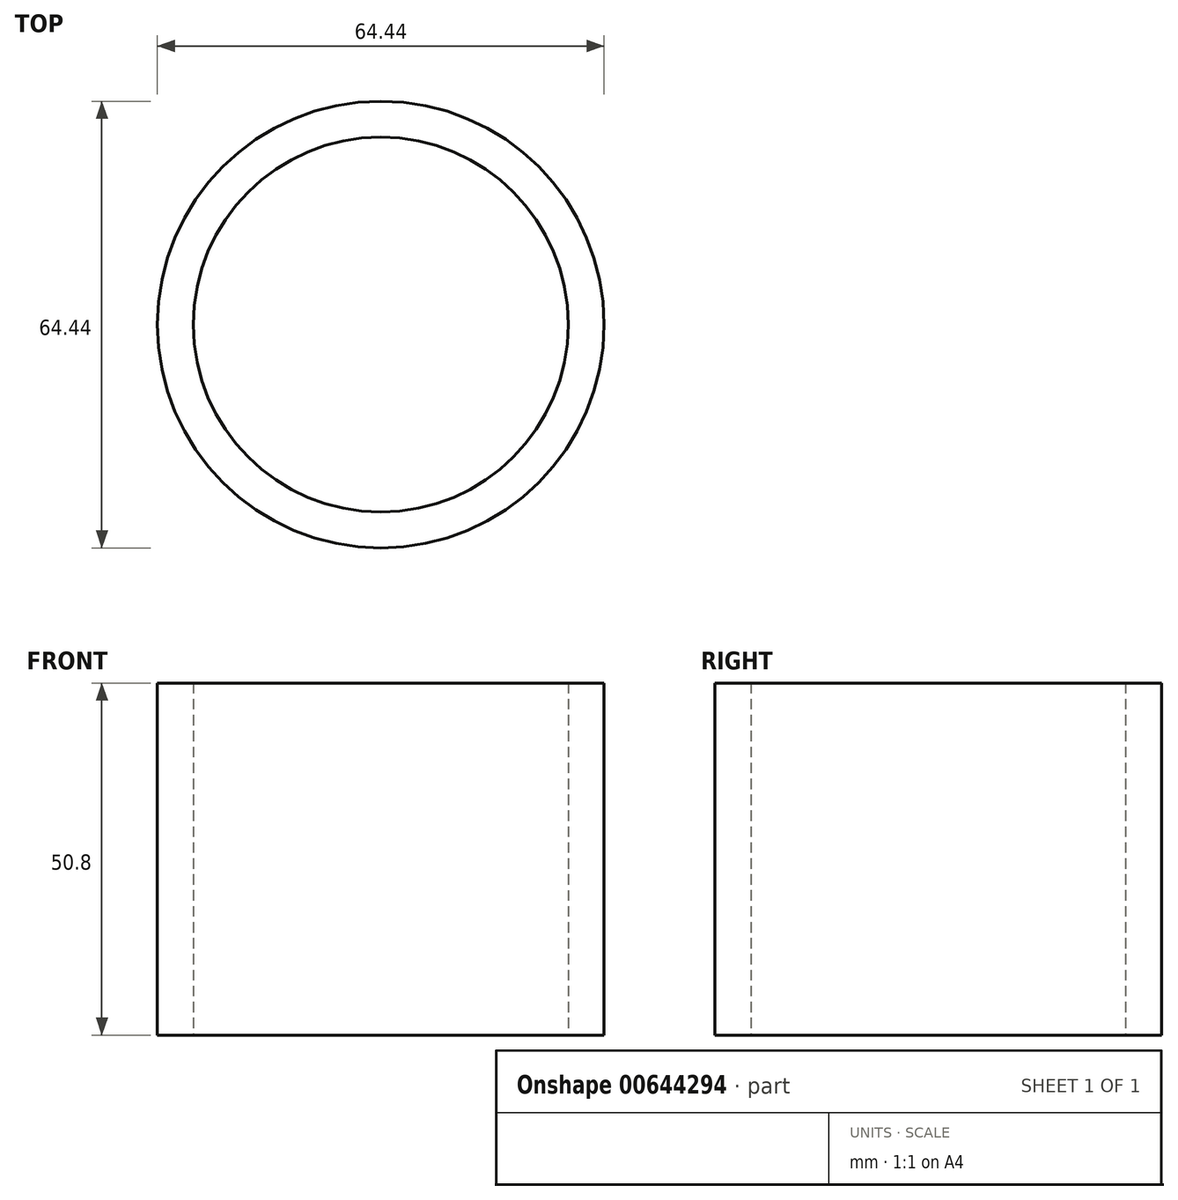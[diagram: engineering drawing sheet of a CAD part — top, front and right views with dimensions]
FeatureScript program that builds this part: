
annotation { "Feature Type Name" : "Feature", "Feature Type Description" : "" }
export const myFeature = defineFeature(function(context is Context, id is Id, definition is map)
    precondition{}
    {
        {
            var Q0;
            Q0=qCreatedBy(makeId("Top.planeOp"),FACE);
            var sketch = newSketch(context, id + "F0", { "sketchPlane" : qUnion([Q0])});
            skCircle(sketch, "E0", {"center": v(0, 0) * mm, "radius": 32.22 * mm});
            skCircle(sketch, "E1", {"center": v(0, 0) * mm, "radius": 27.05 * mm});
            skSolve(sketch);
        }
        {
            var Q0;
            Q0=makeQuery(id+"F0.imprint","IMPRINT",FACE,{"disambiguationData":[TD([[makeQuery(id+"F0.imprint","IMPRINT",EDGE,{"derivedFrom":sQuery(id+"F0.wireOp",EDGE,"E0")}),1.0]])]});
            var Q1;
            Q1=sQuery(id+"F0.wireOp",EDGE,"E0");
            var Q2;
            Q2=sQuery(id+"F0.wireOp",EDGE,"E1");
            extrude(context, id + "F1", {"entities" : qUnion([Q0]), "surfaceEntities" : qUnion([Q1, Q2]), "depth" : 50.8 * mm, "offsetDistance" : 25.4 * mm});
        }
    });
